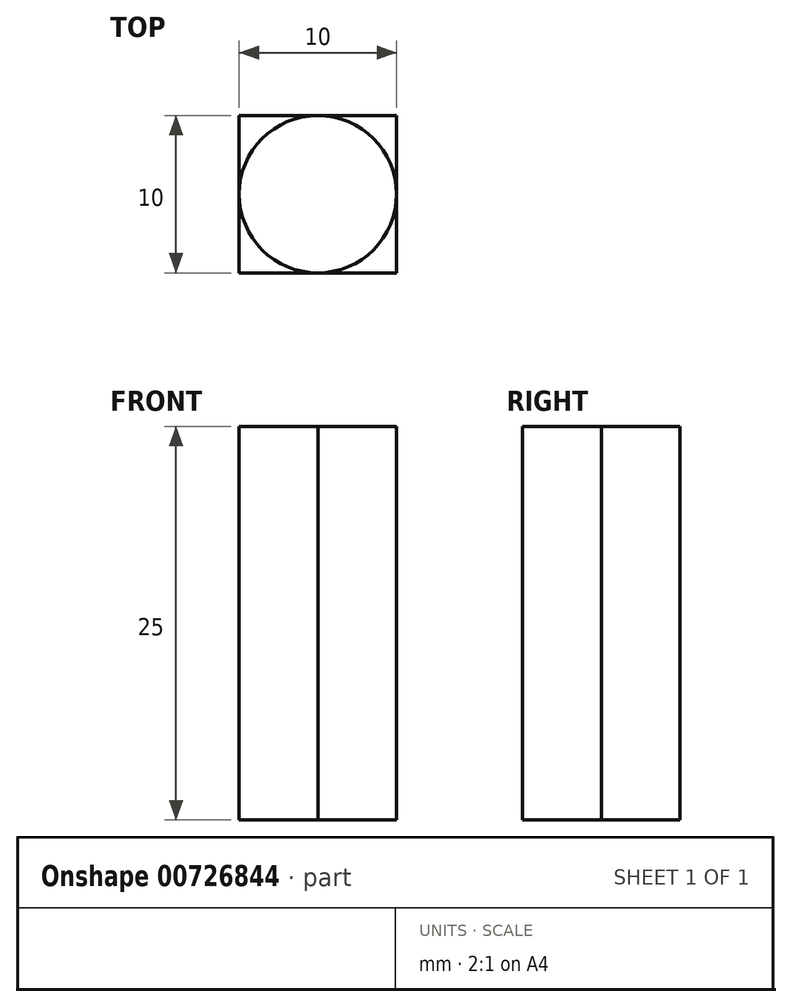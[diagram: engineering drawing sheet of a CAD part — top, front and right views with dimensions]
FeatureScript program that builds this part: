
annotation { "Feature Type Name" : "Feature", "Feature Type Description" : "" }
export const myFeature = defineFeature(function(context is Context, id is Id, definition is map)
    precondition{}
    {
        {
            var Q0;
            Q0=qCreatedBy(makeId("Top.planeOp"),FACE);
            var sketch = newSketch(context, id + "F0", { "sketchPlane" : qUnion([Q0])});
            skLineSegment(sketch, "E0.bottom", {"start": v(-60.51, -1.27) * mm, "end": v(-50.51, -1.27) * mm});
            skLineSegment(sketch, "E0.top", {"start": v(-60.51, -11.27) * mm, "end": v(-50.51, -11.27) * mm});
            skLineSegment(sketch, "E0.left", {"start": v(-60.51, -1.27) * mm, "end": v(-60.51, -11.27) * mm});
            skLineSegment(sketch, "E0.right", {"start": v(-50.51, -1.27) * mm, "end": v(-50.51, -11.27) * mm});
            skCircle(sketch, "E1", {"center": v(-55.51, -6.27) * mm, "radius": 5 * mm});
            skPoint(sketch, "E1.centerSnap0", {"position": v(-55.51, -11.27) * mm});
            skPoint(sketch, "E1.centerSnap1", {"position": v(-60.51, -6.27) * mm});
            skLineSegment(sketch, "E2.bottom", {"start": v(-40.9, 0.93) * mm, "end": v(79.1, 0.93) * mm});
            skLineSegment(sketch, "E2.top", {"start": v(-40.9, -14.07) * mm, "end": v(79.1, -14.07) * mm});
            skLineSegment(sketch, "E2.left", {"start": v(-40.9, 0.93) * mm, "end": v(-40.9, -14.07) * mm});
            skLineSegment(sketch, "E2.right", {"start": v(79.1, 0.93) * mm, "end": v(79.1, -14.07) * mm});
            skLineSegment(sketch, "E3", {"start": v(-40.9, -6.57) * mm, "end": v(79.1, -6.57) * mm});
            skSolve(sketch);
        }
        {
            var Q0;
            {var subQ0=sQuery(id+"F0.wireOp",EDGE,"E0.left");var subQ1=sQuery(id+"F0.wireOp",EDGE,"E0.bottom");var subQ2=makeQuery(id+"F0.imprint","INTERSECT",VERTEX,{"derivedFrom":[subQ1,subQ0]});Q0=makeQuery(id+"F0.imprint","IMPRINT",FACE,{"disambiguationData":[TD([[makeQuery(id+"F0.imprint","IMPRINT",EDGE,{"disambiguationData":[TD([[subQ2,-1.0]])],"derivedFrom":subQ1}),-1.0]])]});}
            var Q1;
            {var subQ0=sQuery(id+"F0.wireOp",EDGE,"E0.right");var subQ1=sQuery(id+"F0.wireOp",EDGE,"E0.bottom");var subQ2=makeQuery(id+"F0.imprint","INTERSECT",VERTEX,{"derivedFrom":[subQ1,subQ0]});Q1=makeQuery(id+"F0.imprint","IMPRINT",FACE,{"disambiguationData":[TD([[makeQuery(id+"F0.imprint","IMPRINT",EDGE,{"disambiguationData":[TD([[subQ2,1.0]])],"derivedFrom":subQ1}),-1.0]])]});}
            var Q2;
            {var subQ0=sQuery(id+"F0.wireOp",EDGE,"E0.left");var subQ1=sQuery(id+"F0.wireOp",EDGE,"E0.top");var subQ2=makeQuery(id+"F0.imprint","INTERSECT",VERTEX,{"derivedFrom":[subQ1,subQ0]});Q2=makeQuery(id+"F0.imprint","IMPRINT",FACE,{"disambiguationData":[TD([[makeQuery(id+"F0.imprint","IMPRINT",EDGE,{"disambiguationData":[TD([[subQ2,-1.0]])],"derivedFrom":subQ1}),1.0]])]});}
            var Q3;
            {var subQ0=sQuery(id+"F0.wireOp",EDGE,"E0.right");var subQ1=sQuery(id+"F0.wireOp",EDGE,"E0.top");var subQ2=makeQuery(id+"F0.imprint","INTERSECT",VERTEX,{"derivedFrom":[subQ1,subQ0]});Q3=makeQuery(id+"F0.imprint","IMPRINT",FACE,{"disambiguationData":[TD([[makeQuery(id+"F0.imprint","IMPRINT",EDGE,{"disambiguationData":[TD([[subQ2,1.0]])],"derivedFrom":subQ1}),1.0]])]});}
            var Q4;
            {var subQ0=sQuery(id+"F0.wireOp",EDGE,"E2.top");Q4=makeQuery(id+"F0.imprint","IMPRINT",FACE,{"disambiguationData":[TD([[makeQuery(id+"F0.imprint","IMPRINT",EDGE,{"derivedFrom":subQ0}),1.0]])]});}
            extrude(context, id + "F1", {"entities" : qUnion([Q0, Q1, Q2, Q3, Q4]), "depth" : 25 * mm, "offsetDistance" : 25 * mm});
        }
        {
            var Q0;
            {var subQ0=sQuery(id+"F0.wireOp",EDGE,"E1");var subQ1=makeQuery(id+"F0.imprint","INTERSECT",VERTEX,{"derivedFrom":[sQuery(id+"F0.wireOp",EDGE,"E0.bottom"),subQ0]});Q0=makeQuery(id+"F0.imprint","IMPRINT",FACE,{"disambiguationData":[TD([[makeQuery(id+"F0.imprint","IMPRINT",EDGE,{"disambiguationData":[TD([[subQ1,1.0]])],"derivedFrom":subQ0}),1.0]])]});}
            var Q1;
            {var subQ0=sQuery(id+"F0.wireOp",EDGE,"E2.bottom");Q1=makeQuery(id+"F0.imprint","IMPRINT",FACE,{"disambiguationData":[TD([[makeQuery(id+"F0.imprint","IMPRINT",EDGE,{"derivedFrom":subQ0}),-1.0]])]});}
            extrude(context, id + "F2", {"entities" : qUnion([Q0, Q1]), "depth" : 25 * mm, "offsetDistance" : 25 * mm});
        }
        {
            var Q0;
            Q0=makeQuery(id+"F2.opExtrude","SWEPT_BODY",BODY,{"disambiguationData":[OSD([sQuery(id+"F0.wireOp",EDGE,"E2.bottom"),sQuery(id+"F0.wireOp",EDGE,"E2.left"),sQuery(id+"F0.wireOp",EDGE,"E2.right"),sQuery(id+"F0.wireOp",EDGE,"E3")])]});
            deleteBodies(context, id + "F3", {"entities" : qUnion([Q0])});
        }
        {
            var Q0;
            Q0=makeQuery(id+"F1.opExtrude","SWEPT_BODY",BODY,{"disambiguationData":[OSD([sQuery(id+"F0.wireOp",EDGE,"E2.top"),sQuery(id+"F0.wireOp",EDGE,"E2.left"),sQuery(id+"F0.wireOp",EDGE,"E2.right"),sQuery(id+"F0.wireOp",EDGE,"E3")])]});
            deleteBodies(context, id + "F4", {"entities" : qUnion([Q0])});
        }
    });
